# Revit family: Towel_Bar-DXV-Contemporary-D35104260_Series
name_source: partatom
category: Specialty Equipment
revit_build: Autodesk Revit 2014 (Build: 20130308_1515(x64)
units: mm (PartAtom-declared; Revit-internal decimal feet)

## types (2) — shared parameters
Assembly Code = C1030200
Default Elevation = 40"
Description = CONTEMPORARY TOWEL RACK
Height = 4 5/8"
Installation Type = Surface Mounted
Length = 8 3/16"
Manufacturer = DXV
Price = Prices may vary. Please consult Manufacturer Representative for most up-to-date price list.
Product Documentation Link = https://dxv01.blob.core.windows.net
Product Page URL = https://www.dxv.com
URL = http://www.dxv.com
Warranty Documentation Link = https://www.dxv.com
Width = 21 5/8"

## per-type parameters (varying)
| type | Finish | Material |
| D35104260.100 | Brass-DXV-100-Polished Chrome | Brass-DXV-100-Polished Chrome |
| D35104260.144 | Brass-DXV-144-Brushed Nickel | Brass-DXV-144-Brushed Nickel |

note: column(s) folded — value = type name in every type: Model

## geometry (parser evidence)
native form markers: Sweep x3
no freeform markers — native parametric forms only
